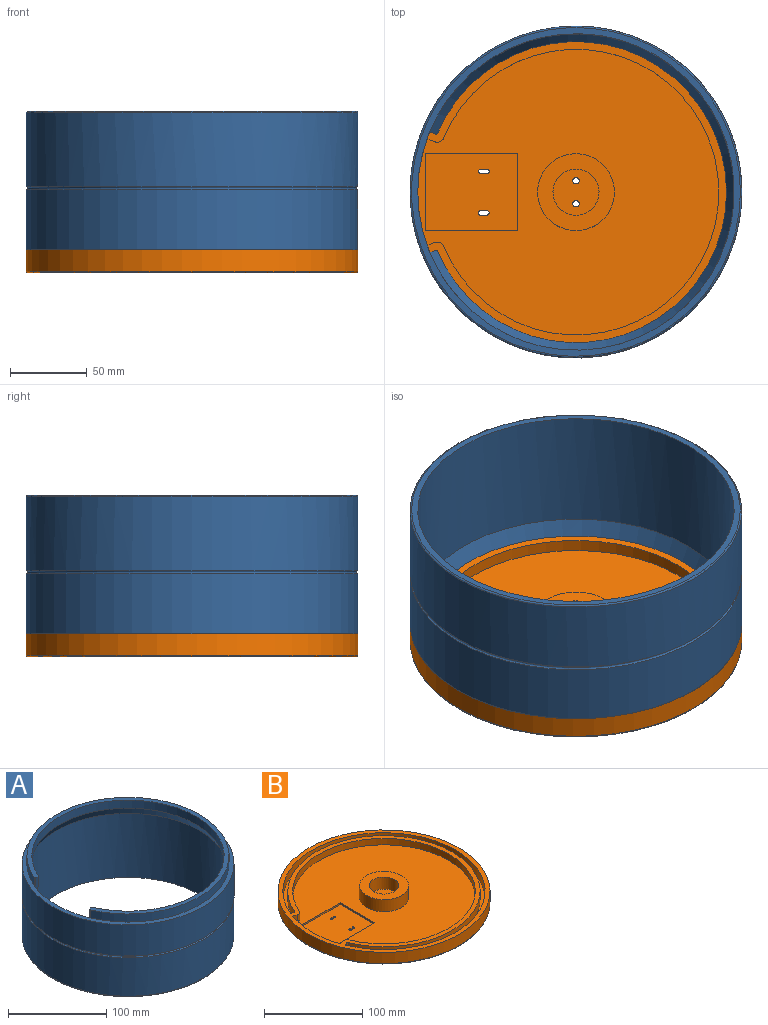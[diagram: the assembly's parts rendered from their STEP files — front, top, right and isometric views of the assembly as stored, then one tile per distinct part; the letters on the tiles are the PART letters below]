
ASSEMBLY  parts=2 mates=1
PART A: 17 faces, bbox 235.3x235.3x100 mm
  f0: cylinder r=103mm len=206mm, axis (0,0,-1), area 52582.4mm2, adj f3,f4,f9,f10,f11
  f1: torus R=108mm, axis (0,0,-1), area 2119.3mm2, adj f2,f5
  f2: cylinder r=108mm len=216mm, axis (0,0,-1), area 26464.8mm2, adj f1,f3
  f3: plane 216x216mm, normal (0,0,1), area 3314.8mm2, adj f0,f2,f6,f10,f11,f13,f14
  f4: plane 214x214mm, normal (0,0,-1), area 2638.9mm2, adj f0,f12
  f5: cylinder r=108mm len=216mm, axis (0,0,-1), area 32572mm2, adj f1,f12
  f6: cylinder r=103mm len=206mm, axis (0,0,-1), area 5642.5mm2, adj f3,f7,f13,f14
  f7: plane 206x197.85mm, normal (0,0,1), area 2761.8mm2, adj f6,f8,f10,f11,f13,f14,f15,f16
  f8: cylinder r=98mm len=196mm, axis (0,0,-1), area 5368mm2, adj f7,f9,f15,f16
  f9: cone r=98mm half-angle=26.6deg, axis (0,0,-1), area 6176.5mm2, adj f0,f8,f10,f11,f15,f16
  f10: plane 20x3.7mm, normal (-0.38,-0.92,0), area 54mm2, adj f0,f3,f7,f9,f13,f16
  f11: plane 20x3.7mm, normal (-0.38,0.92,0), area 54mm2, adj f0,f3,f7,f9,f14,f15
  f12: torus R=107mm, axis (0,0,1), area 1062.3mm2, adj f4,f5
  f13: cylinder r=1mm len=10mm, axis (0,0,-1), area 15.8mm2, adj f3,f6,f7,f10
  f14: cylinder r=1mm len=10mm, axis (0,0,-1), area 15.8mm2, adj f3,f6,f7,f11
  f15: cylinder r=1mm len=11.99mm, axis (0,0,-1), area 16.7mm2, adj f7,f8,f9,f11
  f16: cylinder r=1mm len=11.99mm, axis (0,0,-1), area 16.7mm2, adj f7,f8,f9,f10
PART B: 51 faces, bbox 233.8x233.8x22 mm
  f0: plane 196x186mm, normal (0,0,1), area 22888.3mm2, adj f7,f9,f10,f11,f12,f37,f38,f39
  f1: plane 30x30mm, normal (0,0,1), area 679.1mm2, adj f6,f32,f33
  f2: plane 30x30mm, normal (0,0,-1), area 679.1mm2, adj f31,f32,f33
  f3: plane 60x50mm, normal (0,0,1), area 2961.9mm2, adj f9,f10,f11,f12,f13,f14,f15,f16
  f4: cylinder r=108mm len=216mm, axis (0,0,-1), area 9500.2mm2, adj f44,f46
  f5: plane 214x214mm, normal (0,0,-1), area 35096.7mm2, adj f22,f23,f24,f25,f27,f28,f29,f30
  f6: cylinder r=15mm len=30mm, axis (0,0,-1), area 1413.7mm2, adj f1,f8
  f7: cylinder r=25mm len=50mm, axis (0,0,-1), area 2356.2mm2, adj f0,f8
  f8: plane 50x50mm, normal (0,0,1), area 1256.6mm2, adj f6,f7
  f9: plane 60x2mm, normal (0,1,0), area 120mm2, adj f0,f3,f10,f12
  f10: plane 50x2mm, normal (-1,0,0), area 100mm2, adj f0,f3,f9,f11
  f11: plane 60x2mm, normal (0,-1,0), area 120mm2, adj f0,f3,f10,f12
  f12: plane 50x2mm, normal (1,0,0), area 100mm2, adj f0,f3,f9,f11
  f13: cylinder r=1.5mm len=3mm, axis (0,0,1), area 9.4mm2, adj f3,f14,f16,f26
  f14: plane 4x2mm, normal (0,-1,0), area 8mm2, adj f3,f13,f15,f26
  f15: cylinder r=1.5mm len=3mm, axis (0,0,1), area 9.4mm2, adj f3,f14,f16,f26
  f16: plane 4x2mm, normal (0,1,0), area 8mm2, adj f3,f13,f15,f26
  f17: plane 4x2mm, normal (0,1,0), area 8mm2, adj f3,f18,f20,f21
  f18: cylinder r=1.5mm len=3mm, axis (0,0,1), area 9.4mm2, adj f3,f17,f19,f21
  f19: plane 4x2mm, normal (0,-1,0), area 8mm2, adj f3,f18,f20,f21
  f20: cylinder r=1.5mm len=3mm, axis (0,0,1), area 9.4mm2, adj f3,f17,f19,f21
  f21: plane 12x8mm, normal (0,0,-1), area 63.2mm2, adj f17,f18,f19,f20,f22,f23,f24,f25
  f22: plane 4x3mm, normal (0,1,0), area 12mm2, adj f5,f21,f23,f25
  f23: cylinder r=4mm len=8mm, axis (0,0,1), area 37.7mm2, adj f5,f21,f22,f24
  f24: plane 4x3mm, normal (0,-1,0), area 12mm2, adj f5,f21,f23,f25
  f25: cylinder r=4mm len=8mm, axis (0,0,1), area 37.7mm2, adj f5,f21,f22,f24
  f26: plane 12x8mm, normal (0,0,-1), area 63.2mm2, adj f13,f14,f15,f16,f27,f28,f29,f30
  f27: cylinder r=4mm len=8mm, axis (0,0,1), area 37.7mm2, adj f5,f26,f28,f30
  f28: plane 4x3mm, normal (0,1,0), area 12mm2, adj f5,f26,f27,f29
  f29: cylinder r=4mm len=8mm, axis (0,0,1), area 37.7mm2, adj f5,f26,f28,f30
  f30: plane 4x3mm, normal (0,-1,0), area 12mm2, adj f5,f26,f27,f29
  f31: cylinder r=15mm len=30mm, axis (0,0,-1), area 282.7mm2, adj f2,f5
  f32: cylinder r=2.1mm len=4.2mm, axis (0,0,1), area 52.8mm2, adj f1,f2
  f33: cylinder r=2.1mm len=4.2mm, axis (0,0,1), area 52.8mm2, adj f1,f2
  f34: cylinder r=103mm len=206mm, axis (0,0,-1), area 5642.5mm2, adj f44,f45,f47,f50
  f35: plane 10x2.77mm, normal (0.38,-0.92,0), area 30mm2, adj f44,f45,f47,f48
  f36: cylinder r=98mm len=196mm, axis (0,0,-1), area 5368mm2, adj f44,f45,f48,f49
  f37: cylinder r=93mm len=186mm, axis (0,0,-1), area 4090.4mm2, adj f0,f38,f42,f44
  f38: cylinder r=5mm len=8mm, axis (0,0,-1), area 61.8mm2, adj f0,f37,f39,f44
  f39: plane 8x4.67mm, normal (-0.36,0.93,0), area 40mm2, adj f0,f38,f40,f44
  f40: cylinder r=103mm len=69.26mm, axis (0,0,-1), area 565.1mm2, adj f0,f39,f41,f44
  f41: plane 8x4.67mm, normal (-0.36,-0.93,0), area 40mm2, adj f0,f40,f42,f44
  f42: cylinder r=5mm len=8mm, axis (0,0,-1), area 61.8mm2, adj f0,f37,f41,f44
  f43: plane 10x2.77mm, normal (0.38,0.92,0), area 30mm2, adj f44,f45,f49,f50
  f44: plane 216x216mm, normal (0,0,1), area 6029.9mm2, adj f4,f34,f35,f36,f37,f38,f39,f40
  f45: plane 206x197.85mm, normal (0,0,1), area 2761.8mm2, adj f34,f35,f36,f43,f47,f48,f49,f50
  f46: torus R=107mm, axis (0,0,-1), area 1062.3mm2, adj f4,f5
  f47: cylinder r=1mm len=10mm, axis (0,0,-1), area 15.8mm2, adj f34,f35,f44,f45
  f48: cylinder r=1mm len=10mm, axis (0,0,-1), area 15.6mm2, adj f35,f36,f44,f45
  f49: cylinder r=1mm len=10mm, axis (0,0,-1), area 15.6mm2, adj f36,f43,f44,f45
  f50: cylinder r=1mm len=10mm, axis (0,0,-1), area 15.8mm2, adj f34,f43,f44,f45
PLACE A rot(axis=(1,0,0),180deg) t=(0.78,-0.04,93.26)mm
PLACE B t=(0.78,-0.04,-11.74)mm
MATE fastened A.f7 <-> B.f3  axis (0,0,-1) through (14.81,-0.04,-6.74)mm
